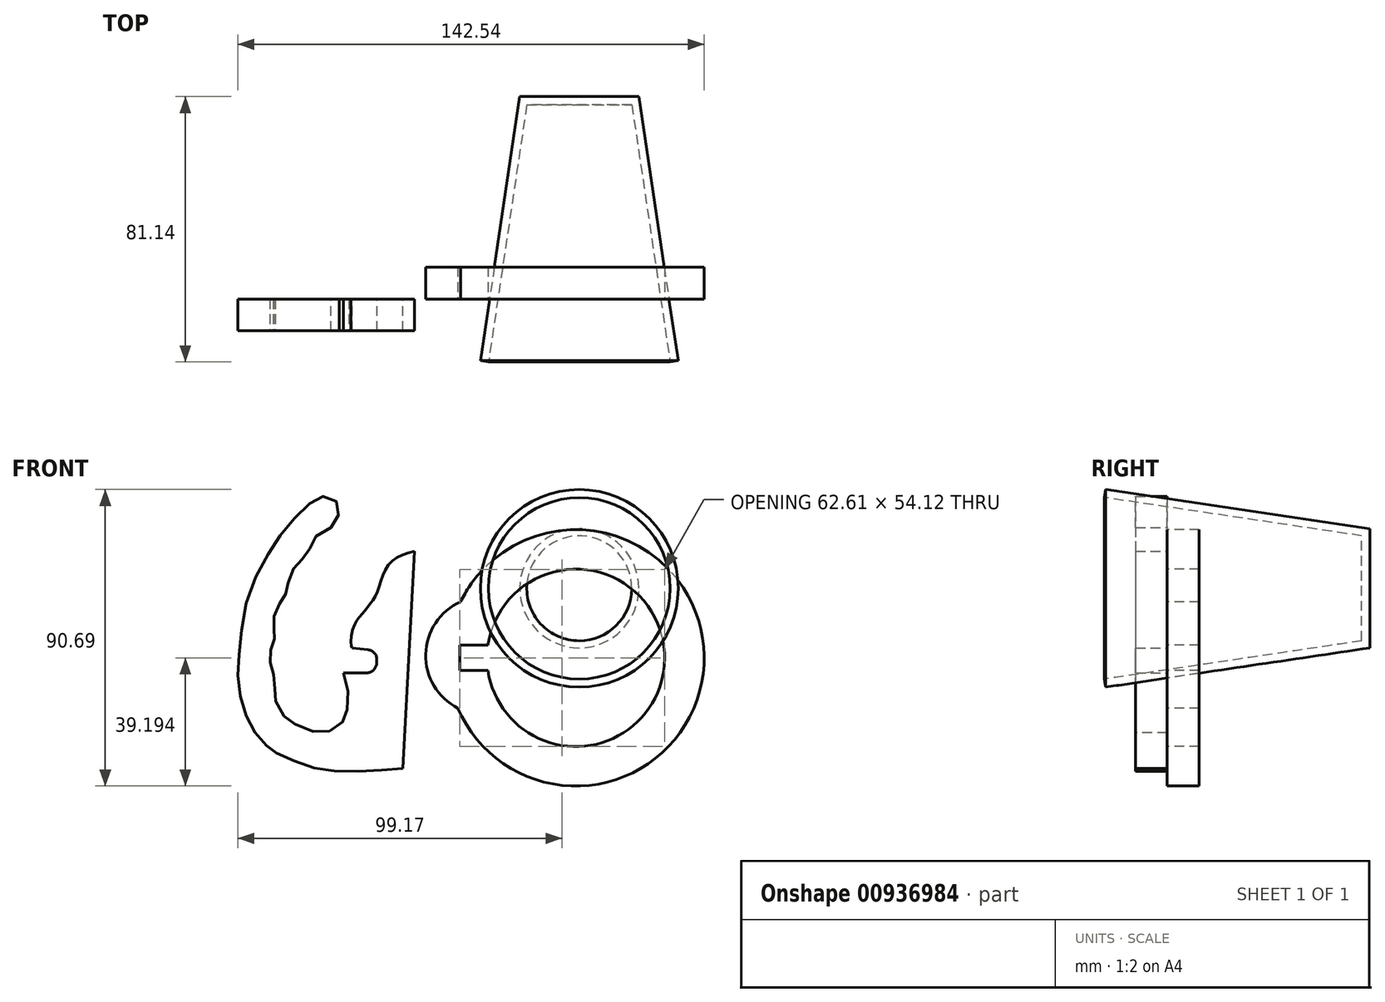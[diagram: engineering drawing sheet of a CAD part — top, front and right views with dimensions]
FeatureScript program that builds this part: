
annotation { "Feature Type Name" : "Feature", "Feature Type Description" : "" }
export const myFeature = defineFeature(function(context is Context, id is Id, definition is map)
    precondition{}
    {
        {
            var Q0;
            Q0=qCreatedBy(makeId("Front.planeOp"),FACE);
            var sketch = newSketch(context, id + "F0", { "sketchPlane" : qUnion([Q0])});
            skFitSpline(sketch, "E0", {"points": [v(-31.33, 18.64) * mm, v(-36.08, 15.77) * mm, v(-37.63, 12.68) * mm, v(-39.17, 9.92) * mm, v(-41.16, 7.82) * mm, v(-43.26, 5.28) * mm, v(-44.59, 1.3) * mm, v(-44.92, -0.8) * mm, v(-45.91, -3.34) * mm, v(-47.57, -5.32) * mm, v(-48.78, -8.53) * mm, v(-49, -11.4) * mm, v(-48.45, -13.94) * mm, v(-48.56, -15.26) * mm, v(-49.56, -17.58) * mm, v(-50, -20.23) * mm, v(-49.89, -23.1) * mm, v(-49, -25.75) * mm, v(-48.56, -29.29) * mm, v(-48.56, -32.6) * mm, v(-47.9, -35.36) * mm, v(-44.8, -40.11) * mm, v(-42.27, -41.55) * mm, v(-35.86, -43.98) * mm, v(-31.11, -43.31) * mm, v(-27.58, -40.55) * mm, v(-26.58, -37.9) * mm, v(-26.03, -32.27) * mm, v(-27.58, -25.83) * mm], "startDerivative": vector(-122.33, -56.1) * mm, "endDerivative": vector(4.35, 100.3) * mm});
            skFitSpline(sketch, "E1", {"points": [v(-31.33, 18.64) * mm, v(-29.12, 22.29) * mm, v(-29.68, 26.48) * mm, v(-33.65, 28.14) * mm, v(-37.85, 25.93) * mm, v(-44.92, 18.64) * mm, v(-50.77, 10.25) * mm, v(-57.07, -3.78) * mm, v(-59.27, -18.47) * mm, v(-59.83, -28.07) * mm, v(-57.95, -37.02) * mm, v(-54.75, -43.87) * mm, v(-50.44, -48.62) * mm, v(-47.9, -50.38) * mm, v(-39.84, -53.92) * mm, v(-31.33, -55.8) * mm, v(-19.4, -55.8) * mm, v(-9.47, -55.02) * mm], "startDerivative": vector(63.18, 78.7) * mm, "endDerivative": vector(145.7, 13.23) * mm});
            skFitSpline(sketch, "E2", {"points": [v(-5.82, 11.35) * mm, v(-11.9, 9.03) * mm, v(-15.32, 4.5) * mm, v(-17.09, -0.9) * mm, v(-19.19, -4.44) * mm, v(-22.6, -8.75) * mm, v(-24.38, -11.5) * mm, v(-25.26, -17.14) * mm, v(-24.93, -18.25) * mm], "startDerivative": vector(-43.9, -11.46) * mm, "endDerivative": vector(6.81, -12.73) * mm});
            skLineSegment(sketch, "E3", {"start": v(-5.82, 11.35) * mm, "end": v(-9.47, -55.02) * mm});
            skLineSegment(sketch, "E4", {"start": v(-27.58, -25.83) * mm, "end": v(-20.43, -25.83) * mm});
            skLineSegment(sketch, "E5", {"start": v(-17.44, -23.05) * mm, "end": v(-17.36, -22) * mm});
            skLineSegment(sketch, "E6", {"start": v(-20.02, -18.8) * mm, "end": v(-24.93, -18.25) * mm});
            skPoint(sketch, "E7.visualSharp", {"position": v(-17.15, -19.12) * mm});
            skArc(sketch, "E7.filletArc", {"start": v(-17.36, -22) * mm, "mid": v(-18.04, -19.86) * mm, "end": v(-20.02, -18.8) * mm});
            skPoint(sketch, "E8.visualSharp", {"position": v(-17.64, -25.83) * mm});
            skArc(sketch, "E8.filletArc", {"start": v(-20.43, -25.83) * mm, "mid": v(-18.39, -25.03) * mm, "end": v(-17.44, -23.05) * mm});
            skSolve(sketch);
        }
        {
            var Q0;
            Q0=makeQuery(id+"F0.imprint","IMPRINT",FACE,{"disambiguationData":[TD([[makeQuery(id+"F0.imprint","IMPRINT",EDGE,{"derivedFrom":sQuery(id+"F0.wireOp",EDGE,"E0")}),-1.0]])]});
            extrude(context, id + "F1", {"entities" : qUnion([Q0]), "depth" : 9.7 * mm, "offsetDistance" : 25 * mm});
        }
        {
            var Q0;
            Q0=makeQuery(id+"F1.opExtrude","CAP_FACE",FACE,{"disambiguationData":[OSD([sQuery(id+"F0.wireOp",EDGE,"E0"),sQuery(id+"F0.wireOp",EDGE,"E1"),sQuery(id+"F0.wireOp",EDGE,"E2"),sQuery(id+"F0.wireOp",EDGE,"E3"),sQuery(id+"F0.wireOp",EDGE,"E4"),sQuery(id+"F0.wireOp",EDGE,"E5"),sQuery(id+"F0.wireOp",EDGE,"E6"),sQuery(id+"F0.wireOp",EDGE,"E7.filletArc"),sQuery(id+"F0.wireOp",EDGE,"E8.filletArc")])],"isStart":true});
            var sketch = newSketch(context, id + "F2", { "sketchPlane" : qUnion([Q0])});
            skArc(sketch, "E9", {"start": v(-8.2, -4.13) * mm, "mid": v(-82.65, -22.23) * mm, "end": v(-7.4, -36.65) * mm});
            skArc(sketch, "E10", {"start": v(-16.61, -17.37) * mm, "mid": v(-70.6, -21.27) * mm, "end": v(-16.61, -25.17) * mm});
            skLineSegment(sketch, "E11.bottom", {"start": v(-16.61, -17.37) * mm, "end": v(-7.99, -17.37) * mm});
            skLineSegment(sketch, "E11.top", {"start": v(-16.61, -25.17) * mm, "end": v(-7.99, -25.17) * mm});
            skLineSegment(sketch, "E12", {"start": v(-7.99, -17.37) * mm, "end": v(-7.99, -25.17) * mm});
            skArc(sketch, "E13", {"start": v(-7.4, -36.65) * mm, "mid": v(2.45, -20.14) * mm, "end": v(-8.2, -4.13) * mm});
            skSolve(sketch);
        }
        {
            var Q0;
            Q0=makeQuery(id+"F2.imprint","IMPRINT",FACE,{"disambiguationData":[TD([[makeQuery(id+"F2.imprint","IMPRINT",EDGE,{"derivedFrom":sQuery(id+"F2.wireOp",EDGE,"E9")}),1.0]])]});
            extrude(context, id + "F3", {"entities" : qUnion([Q0]), "depth" : 9.8 * mm, "offsetDistance" : 25 * mm});
        }
        {
            var Q0;
            Q0=qCreatedBy(makeId("Top.planeOp"),FACE);
            var sketch = newSketch(context, id + "F4", { "sketchPlane" : qUnion([Q0])});
            skLineSegment(sketch, "E14", {"start": v(44.5, -42.25) * mm, "end": v(44.5, 61.94) * mm});
            skLineSegment(sketch, "E15", {"start": v(44.5, 61.94) * mm, "end": v(62.7, 61.94) * mm});
            skLineSegment(sketch, "E16", {"start": v(62.7, 61.94) * mm, "end": v(74.73, -18.84) * mm});
            skLineSegment(sketch, "E17.0", {"start": v(60.55, 59.44) * mm, "end": v(72.26, -19.2) * mm});
            skLineSegment(sketch, "E17.1", {"start": v(38.75, 59.44) * mm, "end": v(60.55, 59.44) * mm});
            skLineSegment(sketch, "E18", {"start": v(74.73, -18.84) * mm, "end": v(72.26, -19.2) * mm});
            skSolve(sketch);
        }
        {
            var Q0;
            {var subQ0=sQuery(id+"F4.wireOp",EDGE,"E15");Q0=makeQuery(id+"F4.imprint","IMPRINT",FACE,{"disambiguationData":[TD([[makeQuery(id+"F4.imprint","IMPRINT",EDGE,{"derivedFrom":subQ0}),-1.0]])]});}
            var Q1;
            Q1=sQuery(id+"F4.wireOp",EDGE,"E14");
            revolve(context, id + "F5", {"surfaceOperationType" : NewSurfaceOperationType.NEW, "entities" : qUnion([Q0]), "axis" : qUnion([Q1]), "revolveType" : RevolveType.FULL});
        }
    });
